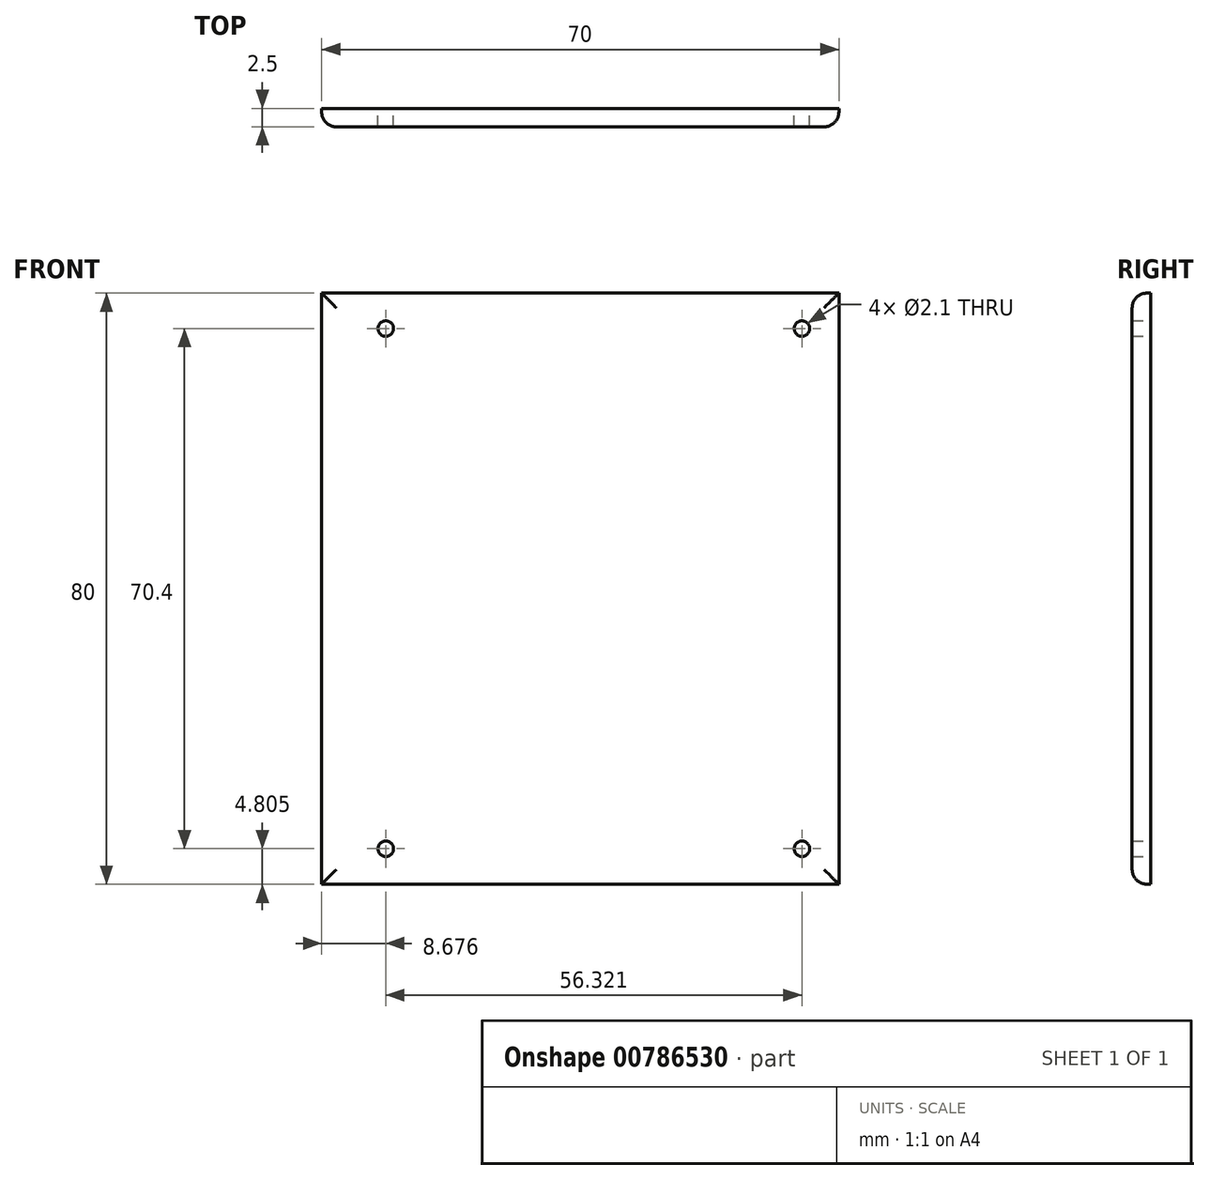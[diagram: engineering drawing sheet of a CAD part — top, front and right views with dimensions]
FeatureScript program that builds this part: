
annotation { "Feature Type Name" : "Feature", "Feature Type Description" : "" }
export const myFeature = defineFeature(function(context is Context, id is Id, definition is map)
    precondition{}
    {
        {
            var Q0;
            Q0=qCreatedBy(makeId("Front.planeOp"),FACE);
            var sketch = newSketch(context, id + "F0", { "sketchPlane" : qUnion([Q0])});
            skLineSegment(sketch, "E0.bottom", {"start": v(-41.52, 53.45) * mm, "end": v(28.48, 53.45) * mm});
            skLineSegment(sketch, "E0.top", {"start": v(-41.52, -26.55) * mm, "end": v(28.48, -26.55) * mm});
            skLineSegment(sketch, "E0.left", {"start": v(-41.52, 53.45) * mm, "end": v(-41.52, -26.55) * mm});
            skLineSegment(sketch, "E0.right", {"start": v(28.48, 53.45) * mm, "end": v(28.48, -26.55) * mm});
            skCircle(sketch, "E1", {"center": v(-32.84, 48.65) * mm, "radius": 1.05 * mm});
            skCircle(sketch, "E2", {"center": v(23.48, 48.65) * mm, "radius": 1.05 * mm});
            skCircle(sketch, "E3.MirrorC", {"center": v(-32.84, -21.75) * mm, "radius": 1.05 * mm});
            skCircle(sketch, "E4.MirrorC", {"center": v(23.48, -21.75) * mm, "radius": 1.05 * mm});
            skSolve(sketch);
        }
        {
            var Q0;
            Q0=makeQuery(id+"F0.imprint","IMPRINT",FACE,{"disambiguationData":[TD([[makeQuery(id+"F0.imprint","IMPRINT",EDGE,{"derivedFrom":sQuery(id+"F0.wireOp",EDGE,"E0.bottom")}),-1.0]])]});
            extrude(context, id + "F1", {"entities" : qUnion([Q0]), "depth" : 2.5 * mm, "offsetDistance" : 25 * mm});
        }
        {
            var Q0;
            Q0=makeQuery(id+"F1.opExtrude","CAP_EDGE",EDGE,{"disambiguationData":[OSD([sQuery(id+"F0.wireOp",EDGE,"E0.bottom")])],"isStart":false});
            var Q1;
            Q1=makeQuery(id+"F1.opExtrude","CAP_EDGE",EDGE,{"disambiguationData":[OSD([sQuery(id+"F0.wireOp",EDGE,"E0.left")])],"isStart":false});
            var Q2;
            Q2=makeQuery(id+"F1.opExtrude","CAP_EDGE",EDGE,{"disambiguationData":[OSD([sQuery(id+"F0.wireOp",EDGE,"E0.top")])],"isStart":false});
            var Q3;
            Q3=makeQuery(id+"F1.opExtrude","CAP_EDGE",EDGE,{"disambiguationData":[OSD([sQuery(id+"F0.wireOp",EDGE,"E0.right")])],"isStart":false});
            fillet(context, id + "F2", {"entities" : qUnion([Q0, Q1, Q2, Q3]), "radius" : 2 * mm, "tangentPropagation" : true, "allowEdgeOverflow" : false});
        }
    });
